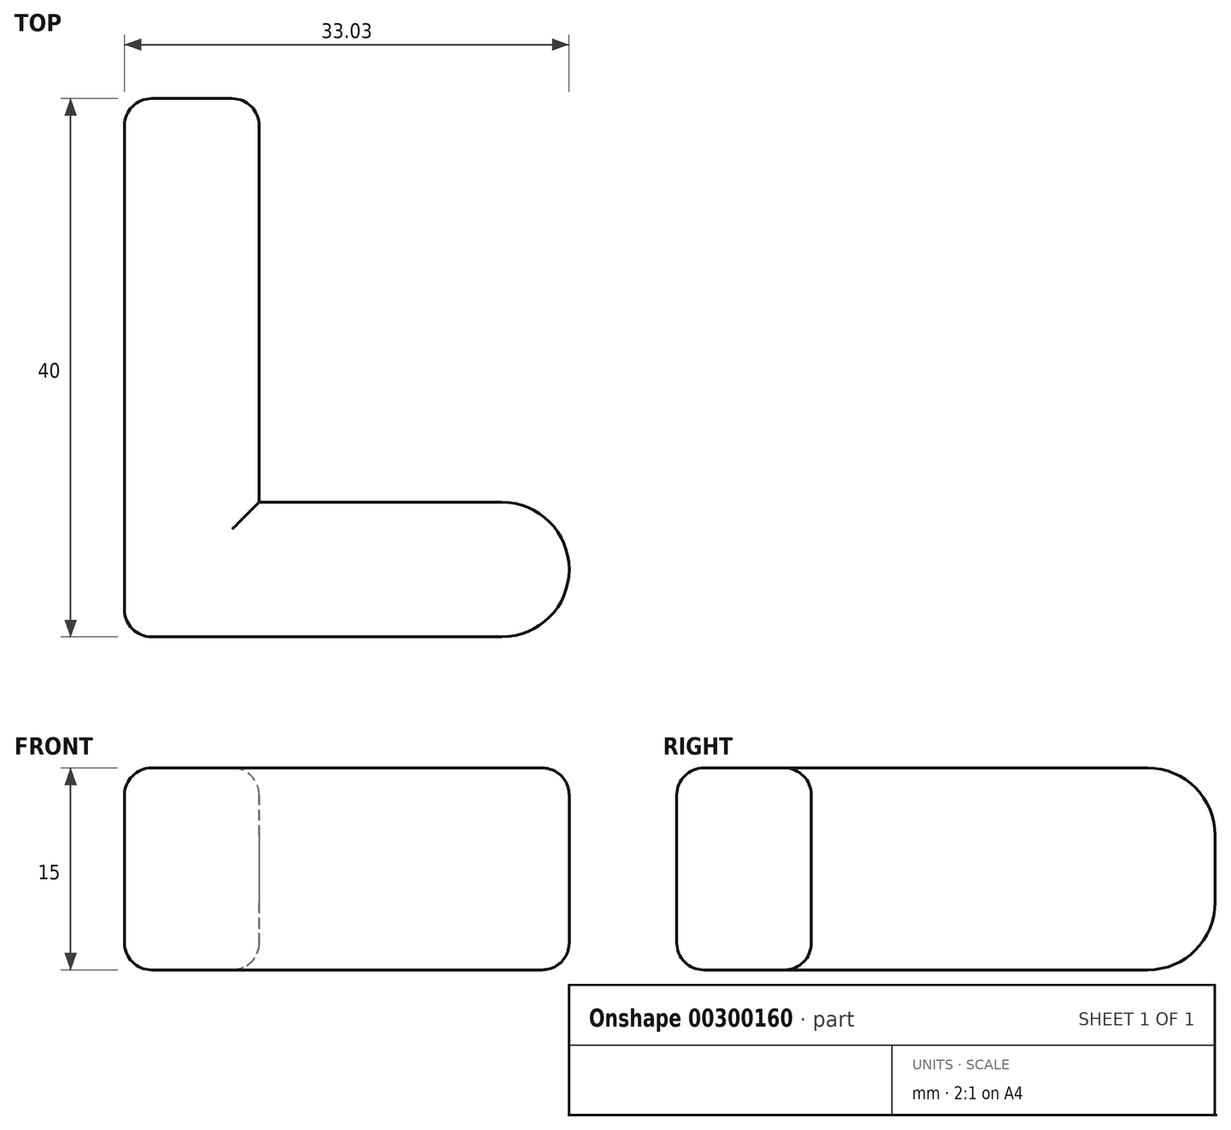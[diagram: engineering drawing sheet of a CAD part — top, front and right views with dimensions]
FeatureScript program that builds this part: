
annotation { "Feature Type Name" : "Feature", "Feature Type Description" : "" }
export const myFeature = defineFeature(function(context is Context, id is Id, definition is map)
    precondition{}
    {
        {
            var Q0;
            Q0=qCreatedBy(makeId("Top.planeOp"),FACE);
            var sketch = newSketch(context, id + "F0", { "sketchPlane" : qUnion([Q0])});
            skLineSegment(sketch, "E0", {"start": v(0, 0) * mm, "end": v(0, 40) * mm});
            skLineSegment(sketch, "E1", {"start": v(0, 40) * mm, "end": v(10, 40) * mm});
            skLineSegment(sketch, "E2", {"start": v(10, 40) * mm, "end": v(10, 10) * mm});
            skLineSegment(sketch, "E3", {"start": v(10, 10) * mm, "end": v(28.03, 10) * mm});
            skLineSegment(sketch, "E4", {"start": v(28.03, 10) * mm, "end": v(28.03, 0) * mm});
            skLineSegment(sketch, "E5", {"start": v(28.03, 0) * mm, "end": v(0, 0) * mm});
            skArc(sketch, "E6", {"start": v(28.03, 0) * mm, "mid": v(33.03, 5) * mm, "end": v(28.03, 10) * mm});
            skSolve(sketch);
        }
        {
            var Q0;
            Q0 = qSketchRegion(id + "F0", true);
            extrude(context, id + "F1", {"entities" : qUnion([Q0]), "depth" : 15 * mm});
        }
        {
            var Q0;
            Q0=makeQuery(id+"F1.opExtrude","CAP_EDGE",EDGE,{"disambiguationData":[OSD([sQuery(id+"F0.wireOp",EDGE,"E2")])],"isStart":false});
            var Q1;
            Q1=makeQuery(id+"F1.opExtrude","CAP_EDGE",EDGE,{"disambiguationData":[OSD([sQuery(id+"F0.wireOp",EDGE,"E3")])],"isStart":false});
            var Q2;
            Q2=makeQuery(id+"F1.opExtrude","CAP_EDGE",EDGE,{"disambiguationData":[OSD([sQuery(id+"F0.wireOp",EDGE,"E5")])],"isStart":true});
            var Q3;
            Q3=makeQuery(id+"F1.opExtrude","SWEPT_EDGE",EDGE,{"disambiguationData":[OSD([sQuery(id+"F0.wireOp",EDGE,"E1"),sQuery(id+"F0.wireOp",EDGE,"E2")])]});
            var Q4;
            Q4=makeQuery(id+"F1.opExtrude","SWEPT_FACE",FACE,{"disambiguationData":[OSD([sQuery(id+"F0.wireOp",EDGE,"E0")])]});
            var Q5;
            Q5=makeQuery(id+"F1.opExtrude","CAP_EDGE",EDGE,{"disambiguationData":[OSD([sQuery(id+"F0.wireOp",EDGE,"E2")])],"isStart":true});
            fillet(context, id + "F2", {"entities" : qUnion([Q0, Q1, Q2, Q3, Q4, Q5]), "radius" : 2 * mm, "tangentPropagation" : true, "allowEdgeOverflow" : false});
        }
        {
            var Q0;
            Q0=makeQuery(id+"F1.opExtrude","SWEPT_FACE",FACE,{"disambiguationData":[OSD([sQuery(id+"F0.wireOp",EDGE,"E1")])]});
            fillet(context, id + "F3", {"entities" : qUnion([Q0]), "radius" : 5 * mm, "tangentPropagation" : true, "allowEdgeOverflow" : false});
        }
    });
